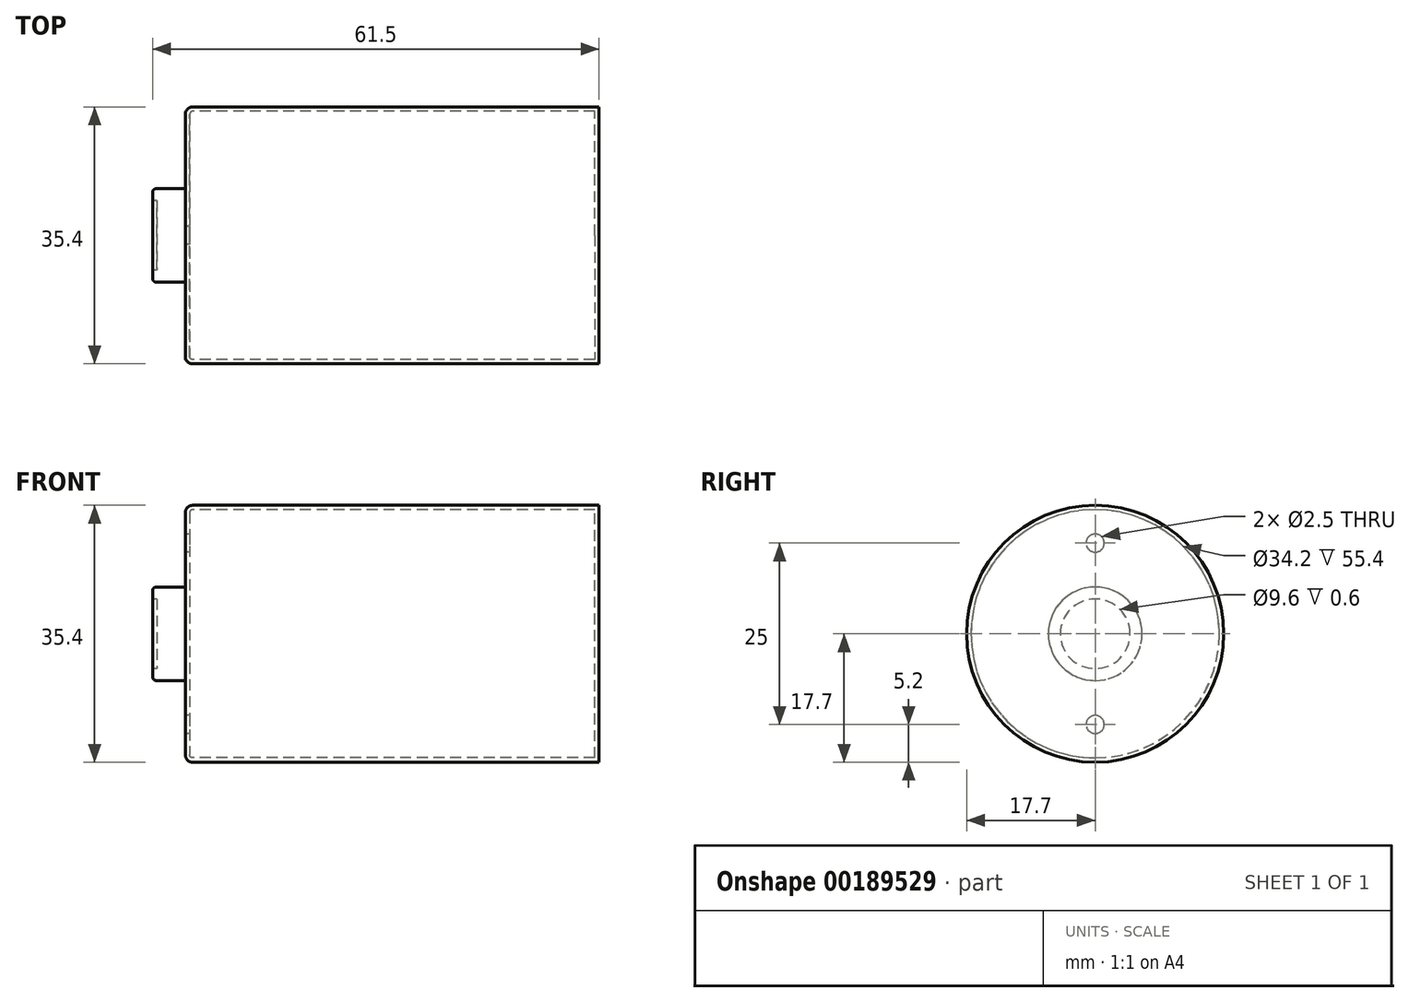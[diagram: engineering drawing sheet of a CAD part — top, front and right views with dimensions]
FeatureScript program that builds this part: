
annotation { "Feature Type Name" : "Feature", "Feature Type Description" : "" }
export const myFeature = defineFeature(function(context is Context, id is Id, definition is map)
    precondition{}
    {
        {
            var Q0;
            Q0=qCreatedBy(makeId("Top.planeOp"),FACE);
            var sketch = newSketch(context, id + "F0", { "sketchPlane" : qUnion([Q0])});
            skLineSegment(sketch, "E0.bottom", {"start": v(0, 0) * mm, "end": v(0.6, 0) * mm});
            skLineSegment(sketch, "E0.top", {"start": v(0, 17.1) * mm, "end": v(0.6, 17.1) * mm});
            skLineSegment(sketch, "E0.left", {"start": v(0, 0) * mm, "end": v(0, 17.1) * mm});
            skLineSegment(sketch, "E0.right", {"start": v(0.6, 0) * mm, "end": v(0.6, 17.1) * mm});
            skLineSegment(sketch, "E1.bottom", {"start": v(0, 17.1) * mm, "end": v(57, 17.1) * mm});
            skLineSegment(sketch, "E1.top", {"start": v(0, 17.7) * mm, "end": v(57, 17.7) * mm});
            skLineSegment(sketch, "E1.left", {"start": v(0, 17.1) * mm, "end": v(0, 17.7) * mm});
            skLineSegment(sketch, "E1.right", {"start": v(57, 17.1) * mm, "end": v(57, 17.7) * mm});
            skSolve(sketch);
        }
        {
            var Q0;
            Q0=makeQuery(id+"F0.imprint","IMPRINT",FACE,{"disambiguationData":[TD([[makeQuery(id+"F0.imprint","IMPRINT",EDGE,{"derivedFrom":sQuery(id+"F0.wireOp",EDGE,"E0.bottom")}),1.0]])]});
            var Q1;
            Q1=makeQuery(id+"F0.imprint","IMPRINT",FACE,{"disambiguationData":[TD([[makeQuery(id+"F0.imprint","IMPRINT",EDGE,{"derivedFrom":sQuery(id+"F0.wireOp",EDGE,"E1.top")}),-1.0]])]});
            var Q2;
            Q2=sQuery(id+"F0.wireOp",EDGE,"E0.bottom");
            revolve(context, id + "F1", {"entities" : qUnion([Q0, Q1]), "axis" : qUnion([Q2]), "revolveType" : RevolveType.FULL});
        }
        {
            var Q0;
            Q0=makeQuery(id+"F1.opRevolve","SWEPT_EDGE",EDGE,{"disambiguationData":[OSD([sQuery(id+"F0.wireOp",EDGE,"E0.right"),sQuery(id+"F0.wireOp",EDGE,"E1.bottom")])]});
            fillet(context, id + "F2", {"entities" : qUnion([Q0]), "radius" : 0.4 * mm, "tangentPropagation" : true, "allowEdgeOverflow" : false});
        }
        {
            var Q0;
            Q0=makeQuery(id+"F1.opRevolve","SWEPT_FACE",FACE,{"disambiguationData":[OSD([sQuery(id+"F0.wireOp",EDGE,"E0.left"),sQuery(id+"F0.wireOp",EDGE,"E1.left")])]});
            fillet(context, id + "F3", {"entities" : qUnion([Q0]), "radius" : 1 * mm, "tangentPropagation" : true, "allowEdgeOverflow" : false});
        }
        {
            var Q0;
            Q0=qCreatedBy(makeId("Right.planeOp"),FACE);
            var sketch = newSketch(context, id + "F4", { "sketchPlane" : qUnion([Q0])});
            skCircle(sketch, "E2", {"center": v(0, 0) * mm, "radius": 6.45 * mm});
            skCircle(sketch, "E3", {"center": v(0, -12.5) * mm, "radius": 1.25 * mm});
            skCircle(sketch, "E4", {"center": v(0, 12.5) * mm, "radius": 1.25 * mm});
            skSolve(sketch);
        }
        {
            var Q0;
            Q0=makeQuery(id+"F4.imprint","IMPRINT",FACE,{"disambiguationData":[TD([[makeQuery(id+"F4.imprint","IMPRINT",EDGE,{"derivedFrom":sQuery(id+"F4.wireOp",EDGE,"E2")}),1.0]])]});
            extrude(context, id + "F5", {"entities" : qUnion([Q0]), "operationType" : NewBodyOperationType.ADD, "oppositeDirection" : true, "depth" : 4.5 * mm});
        }
        {
            var Q0;
            Q0=makeQuery(id+"F5.opExtrude","CAP_EDGE",EDGE,{"disambiguationData":[OSD([sQuery(id+"F4.wireOp",EDGE,"E2")])],"isStart":true});
            var Q1;
            Q1=makeQuery(id+"F5.opExtrude","CAP_EDGE",EDGE,{"disambiguationData":[OSD([sQuery(id+"F4.wireOp",EDGE,"E2")])],"isStart":false});
            fillet(context, id + "F6", {"entities" : qUnion([Q0, Q1]), "radius" : 0.5 * mm, "tangentPropagation" : true, "allowEdgeOverflow" : false});
        }
        {
            var Q0;
            Q0=makeQuery(id+"F5.opExtrude","CAP_FACE",FACE,{"disambiguationData":[OSD([sQuery(id+"F4.wireOp",EDGE,"E2")])],"isStart":false});
            var sketch = newSketch(context, id + "F7", { "sketchPlane" : qUnion([Q0])});
            skCircle(sketch, "E5", {"center": v(0, 0) * mm, "radius": 4.8 * mm});
            skSolve(sketch);
        }
        {
            var Q0;
            Q0=makeQuery(id+"F7.imprint","IMPRINT",FACE,{"disambiguationData":[TD([[makeQuery(id+"F7.imprint","IMPRINT",EDGE,{"derivedFrom":sQuery(id+"F7.wireOp",EDGE,"E5")}),1.0]])]});
            extrude(context, id + "F8", {"entities" : qUnion([Q0]), "operationType" : NewBodyOperationType.REMOVE, "oppositeDirection" : true, "depth" : 0.6 * mm});
        }
        {
            var Q0;
            Q0=makeQuery(id+"F4.imprint","IMPRINT",FACE,{"disambiguationData":[TD([[makeQuery(id+"F4.imprint","IMPRINT",EDGE,{"derivedFrom":sQuery(id+"F4.wireOp",EDGE,"E3")}),1.0]])]});
            var Q1;
            Q1=makeQuery(id+"F4.imprint","IMPRINT",FACE,{"disambiguationData":[TD([[makeQuery(id+"F4.imprint","IMPRINT",EDGE,{"derivedFrom":sQuery(id+"F4.wireOp",EDGE,"E4")}),1.0]])]});
            extrude(context, id + "F9", {"entities" : qUnion([Q0, Q1]), "operationType" : NewBodyOperationType.REMOVE, "depth" : 25 * mm});
        }
        {
            var Q0;
            Q0=makeQuery(id+"F1.opRevolve","SWEPT_FACE",FACE,{"disambiguationData":[OSD([sQuery(id+"F0.wireOp",EDGE,"E1.right")])]});
            var sketch = newSketch(context, id + "F10", { "sketchPlane" : qUnion([Q0])});
            skSolve(sketch);
        }
        {
            var Q0;
            Q0=makeQuery(id+"F10.imprint","IMPRINT",FACE,{"disambiguationData":[TD([[makeQuery(id+"F10.imprint","IMPRINT",EDGE,{"derivedFrom":makeQuery(id+"F1.opRevolve","SWEPT_EDGE",EDGE,{"disambiguationData":[OSD([sQuery(id+"F0.wireOp",EDGE,"E1.bottom"),sQuery(id+"F0.wireOp",EDGE,"E1.right")])]})}),-1.0]])]});
            extrude(context, id + "F11", {"entities" : qUnion([Q0]), "operationType" : NewBodyOperationType.ADD, "oppositeDirection" : true, "depth" : 0.6 * mm});
        }
    });
